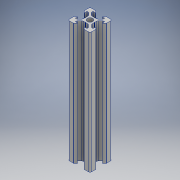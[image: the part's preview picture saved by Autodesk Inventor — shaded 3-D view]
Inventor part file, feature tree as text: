
AUTODESK INVENTOR PART (.ipt)
format: ipt  version: 2020 (Build 240168000, 168)  size: 275,456 bytes
history: native  units: mm
features: other x1, extrude x1, sketch x1
ambient origin geometry x8: Origin, YZ Plane, XZ Plane, XY Plane, X Axis, Y Axis, Z Axis, Center Point
bodies: Body1 (feature_tree)
feature tree (3):
  other  "Твердое тело1"
  extrude  "Выдавливание1"  Depth=0.25mm
  sketch  "Эскиз1"
